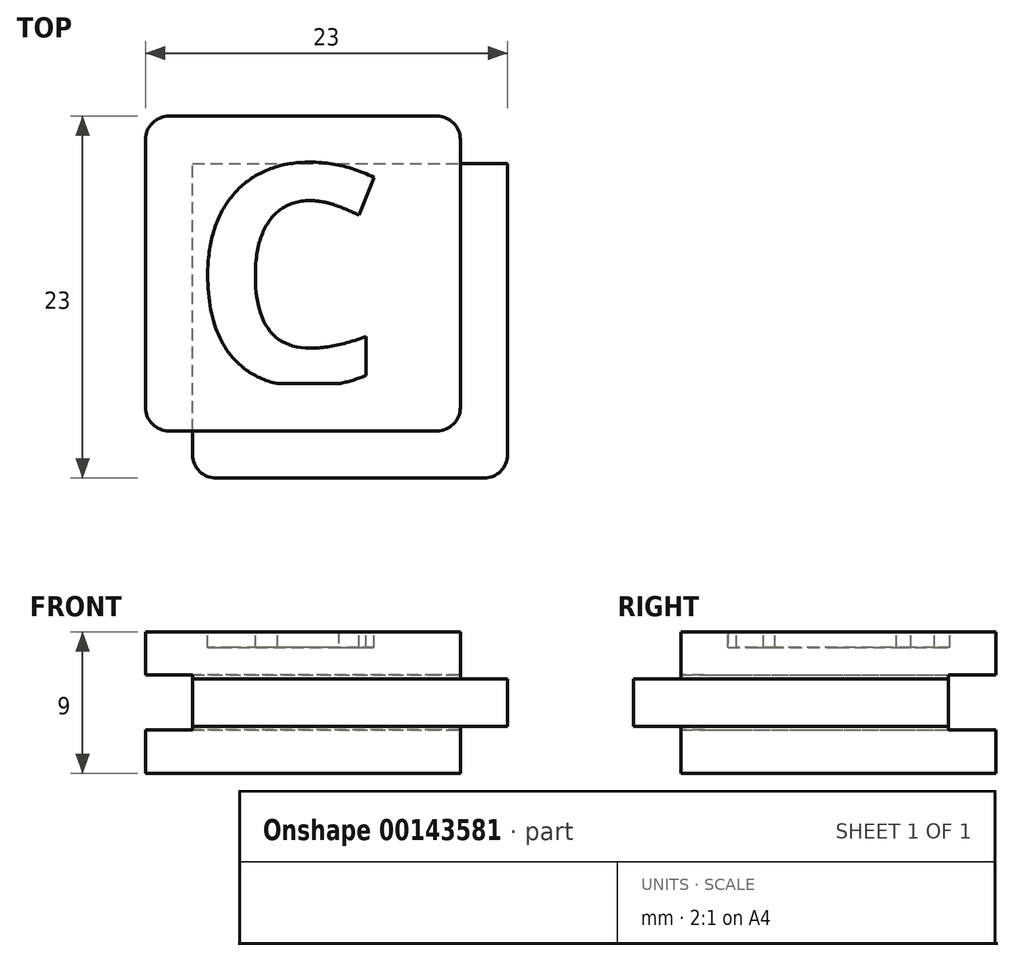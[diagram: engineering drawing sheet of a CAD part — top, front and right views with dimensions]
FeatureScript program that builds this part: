
annotation { "Feature Type Name" : "Feature", "Feature Type Description" : "" }
export const myFeature = defineFeature(function(context is Context, id is Id, definition is map)
    precondition{}
    {
        {
            var Q0;
            Q0=qCreatedBy(makeId("Front.planeOp"),FACE);
            var sketch = newSketch(context, id + "F0", { "sketchPlane" : qUnion([Q0])});
            skLineSegment(sketch, "E0.bottom", {"start": v(10, 4.5) * mm, "end": v(-10, 4.5) * mm});
            skLineSegment(sketch, "E0.top", {"start": v(10, -4.5) * mm, "end": v(-10, -4.5) * mm});
            skLineSegment(sketch, "E0.left", {"start": v(10, 4.5) * mm, "end": v(10, -4.5) * mm});
            skLineSegment(sketch, "E0.right", {"start": v(-10, 4.5) * mm, "end": v(-10, -4.5) * mm});
            skPoint(sketch, "E0.middle", {"position": v(0, 0) * mm});
            skLineSegment(sketch, "E1.bottom", {"start": v(13, 1.5) * mm, "end": v(7, 1.5) * mm});
            skLineSegment(sketch, "E1.top", {"start": v(13, -1.5) * mm, "end": v(7, -1.5) * mm});
            skLineSegment(sketch, "E1.left", {"start": v(13, 1.5) * mm, "end": v(13, -1.5) * mm});
            skLineSegment(sketch, "E1.right", {"start": v(7, 1.5) * mm, "end": v(7, -1.5) * mm});
            skPoint(sketch, "E1.middle", {"position": v(10, 0) * mm});
            skLineSegment(sketch, "E2.bottom", {"start": v(7, 1.5) * mm, "end": v(-7, 1.5) * mm});
            skLineSegment(sketch, "E2.top", {"start": v(7, -1.5) * mm, "end": v(-7, -1.5) * mm});
            skLineSegment(sketch, "E2.right", {"start": v(-7, 1.5) * mm, "end": v(-7, -1.5) * mm});
            skLineSegment(sketch, "E3.bottom", {"start": v(-7, -1.5) * mm, "end": v(-10, -1.5) * mm});
            skLineSegment(sketch, "E3.top", {"start": v(-7, 1.5) * mm, "end": v(-10, 1.5) * mm});
            skLineSegment(sketch, "E3.left", {"start": v(-7, -1.5) * mm, "end": v(-7, 1.5) * mm});
            skLineSegment(sketch, "E3.right", {"start": v(-10, -1.5) * mm, "end": v(-10, 1.5) * mm});
            skSolve(sketch);
        }
        {
            var Q0;
            {var subQ5=sQuery(id+"F0.wireOp",EDGE,"E0.bottom");Q0=makeQuery(id+"F0.imprint","IMPRINT",FACE,{"disambiguationData":[TD([[makeQuery(id+"F0.imprint","IMPRINT",EDGE,{"derivedFrom":subQ5}),1.0]])]});}
            var Q1;
            Q1=makeQuery(id+"F0.imprint","IMPRINT",FACE,{"disambiguationData":[TD([[makeQuery(id+"F0.imprint","IMPRINT",EDGE,{"derivedFrom":sQuery(id+"F0.wireOp",EDGE,"E2.bottom")}),1.0]])]});
            var Q2;
            {var subQ5=sQuery(id+"F0.wireOp",EDGE,"E1.left");Q2=makeQuery(id+"F0.imprint","IMPRINT",FACE,{"disambiguationData":[TD([[makeQuery(id+"F0.imprint","IMPRINT",EDGE,{"derivedFrom":subQ5}),-1.0]])]});}
            var Q3;
            {var subQ5=sQuery(id+"F0.wireOp",EDGE,"E1.right");Q3=makeQuery(id+"F0.imprint","IMPRINT",FACE,{"disambiguationData":[TD([[makeQuery(id+"F0.imprint","IMPRINT",EDGE,{"derivedFrom":subQ5}),1.0]])]});}
            var Q4;
            Q4=makeQuery(id+"F0.imprint","IMPRINT",FACE,{"disambiguationData":[TD([[makeQuery(id+"F0.imprint","IMPRINT",EDGE,{"derivedFrom":sQuery(id+"F0.wireOp",EDGE,"E3.bottom")}),-1.0]])]});
            var Q5;
            {var subQ5=sQuery(id+"F0.wireOp",EDGE,"E0.top");Q5=makeQuery(id+"F0.imprint","IMPRINT",FACE,{"disambiguationData":[TD([[makeQuery(id+"F0.imprint","IMPRINT",EDGE,{"derivedFrom":subQ5}),-1.0]])]});}
            extrude(context, id + "F1", {"entities" : qUnion([Q0, Q1, Q2, Q3, Q4, Q5]), "oppositeDirection" : true, "depth" : 20 * mm});
        }
        {
            var Q0;
            Q0=makeQuery(id+"F0.imprint","IMPRINT",FACE,{"disambiguationData":[TD([[makeQuery(id+"F0.imprint","IMPRINT",EDGE,{"derivedFrom":sQuery(id+"F0.wireOp",EDGE,"E3.bottom")}),-1.0]])]});
            var Q1;
            Q1=makeQuery(id+"F0.imprint","IMPRINT",FACE,{"disambiguationData":[TD([[makeQuery(id+"F0.imprint","IMPRINT",EDGE,{"derivedFrom":sQuery(id+"F0.wireOp",EDGE,"E2.bottom")}),1.0]])]});
            var Q2;
            {var subQ5=sQuery(id+"F0.wireOp",EDGE,"E1.right");Q2=makeQuery(id+"F0.imprint","IMPRINT",FACE,{"disambiguationData":[TD([[makeQuery(id+"F0.imprint","IMPRINT",EDGE,{"derivedFrom":subQ5}),1.0]])]});}
            var Q3;
            {var subQ5=sQuery(id+"F0.wireOp",EDGE,"E1.left");Q3=makeQuery(id+"F0.imprint","IMPRINT",FACE,{"disambiguationData":[TD([[makeQuery(id+"F0.imprint","IMPRINT",EDGE,{"derivedFrom":subQ5}),-1.0]])]});}
            extrude(context, id + "F2", {"entities" : qUnion([Q0, Q1, Q2, Q3]), "operationType" : NewBodyOperationType.ADD, "depth" : 3 * mm});
        }
        {
            var Q0;
            {var subQ0=sQuery(id+"F0.wireOp",EDGE,"E1.left");Q0=makeQuery(id+"F2.boolean.opBoolean","MERGE",FACE,{"derivedFrom":[makeQuery(id+"F1.opExtrude","SWEPT_FACE",FACE,{"disambiguationData":[OSD([subQ0])]}),makeQuery(id+"F2.opExtrude","SWEPT_FACE",FACE,{"disambiguationData":[OSD([subQ0])]})]});}
            var sketch = newSketch(context, id + "F3", { "sketchPlane" : qUnion([Q0])});
            skLineSegment(sketch, "E4.bottom", {"start": v(23, 1.75) * mm, "end": v(17, 1.75) * mm});
            skLineSegment(sketch, "E4.top", {"start": v(23, -1.75) * mm, "end": v(17, -1.75) * mm});
            skLineSegment(sketch, "E4.left", {"start": v(23, 1.75) * mm, "end": v(23, -1.75) * mm});
            skLineSegment(sketch, "E4.right", {"start": v(17, 1.75) * mm, "end": v(17, -1.75) * mm});
            skPoint(sketch, "E4.middle", {"position": v(20, 0) * mm});
            skSolve(sketch);
        }
        {
            var Q0;
            {var subQ1=sQuery(id+"F3.wireOp",EDGE,"E4.bottom");Q0=makeQuery(id+"F3.imprint","IMPRINT",FACE,{"disambiguationData":[TD([[makeQuery(id+"F3.imprint","IMPRINT",EDGE,{"derivedFrom":subQ1}),1.0]])]});}
            var Q1;
            {var subQ1=sQuery(id+"F0.wireOp",EDGE,"E1.left");var subQ8=makeQuery(id+"F1.opExtrude","CAP_EDGE",EDGE,{"disambiguationData":[OSD([subQ1])],"isStart":false});Q1=makeQuery(id+"F3.imprint","IMPRINT",FACE,{"disambiguationData":[TD([[makeQuery(id+"F3.imprint","IMPRINT",EDGE,{"derivedFrom":subQ8}),-1.0]])]});}
            extrude(context, id + "F4", {"entities" : qUnion([Q0, Q1]), "operationType" : NewBodyOperationType.REMOVE, "oppositeDirection" : true, "depth" : 100 * mm});
        }
        {
            var Q0;
            Q0=makeQuery(id+"F4.boolean.opBoolean","COPY",FACE,{"derivedFrom":makeQuery(id+"F4.opExtrude","SWEPT_FACE",FACE,{"disambiguationData":[OSD([sQuery(id+"F3.wireOp",EDGE,"E4.right")])]})});
            var sketch = newSketch(context, id + "F5", { "sketchPlane" : qUnion([Q0])});
            skLineSegment(sketch, "E5.bottom", {"start": v(13, 1.75) * mm, "end": v(7, 1.75) * mm});
            skLineSegment(sketch, "E5.top", {"start": v(13, -1.75) * mm, "end": v(7, -1.75) * mm});
            skLineSegment(sketch, "E5.left", {"start": v(13, 1.75) * mm, "end": v(13, -1.75) * mm});
            skLineSegment(sketch, "E5.right", {"start": v(7, 1.75) * mm, "end": v(7, -1.75) * mm});
            skPoint(sketch, "E5.middle", {"position": v(10, 0) * mm});
            skSolve(sketch);
        }
        {
            var Q0;
            {var subQ3=sQuery(id+"F5.wireOp",EDGE,"E5.left");Q0=makeQuery(id+"F5.imprint","IMPRINT",FACE,{"disambiguationData":[TD([[makeQuery(id+"F5.imprint","IMPRINT",EDGE,{"derivedFrom":subQ3}),-1.0]])]});}
            var Q1;
            {var subQ4=sQuery(id+"F5.wireOp",EDGE,"E5.right");Q1=makeQuery(id+"F5.imprint","IMPRINT",FACE,{"disambiguationData":[TD([[makeQuery(id+"F5.imprint","IMPRINT",EDGE,{"derivedFrom":subQ4}),1.0]])]});}
            extrude(context, id + "F6", {"entities" : qUnion([Q0, Q1]), "operationType" : NewBodyOperationType.REMOVE, "oppositeDirection" : true, "depth" : 100 * mm});
        }
        {
            var Q0;
            Q0=makeQuery(id+"F6.boolean.opBoolean","INTERSECT",EDGE,{"derivedFrom":[makeQuery(id+"F2.opExtrude","CAP_FACE",FACE,{"disambiguationData":[OSD([sQuery(id+"F0.wireOp",EDGE,"E1.bottom"),sQuery(id+"F0.wireOp",EDGE,"E1.top"),sQuery(id+"F0.wireOp",EDGE,"E1.left"),sQuery(id+"F0.wireOp",EDGE,"E2.bottom"),sQuery(id+"F0.wireOp",EDGE,"E2.top"),sQuery(id+"F0.wireOp",EDGE,"E3.bottom"),sQuery(id+"F0.wireOp",EDGE,"E3.top"),sQuery(id+"F0.wireOp",EDGE,"E3.right")])],"isStart":false}),makeQuery(id+"F6.opExtrude","SWEPT_FACE",FACE,{"disambiguationData":[OSD([sQuery(id+"F5.wireOp",EDGE,"E5.right")])]})]});
            var Q1;
            Q1=makeQuery(id+"F2.opExtrude","CAP_EDGE",EDGE,{"disambiguationData":[OSD([sQuery(id+"F0.wireOp",EDGE,"E1.left")])],"isStart":false});
            var Q2;
            {var subQ0=sQuery(id+"F0.wireOp",EDGE,"E0.left");Q2=makeQuery(id+"F1.opExtrude","CAP_EDGE",EDGE,{"disambiguationData":[OSD([subQ0]),TDD([makeQuery(id+"F0.imprint","IMPRINT",EDGE,{"disambiguationData":[TD([[makeQuery(id+"F0.imprint","INTERSECT",VERTEX,{"derivedFrom":[sQuery(id+"F0.wireOp",EDGE,"E0.bottom"),subQ0]}),-1.0]])],"derivedFrom":subQ0})])],"isStart":true});}
            var Q3;
            {var subQ0=sQuery(id+"F0.wireOp",EDGE,"E0.left");Q3=makeQuery(id+"F1.opExtrude","CAP_EDGE",EDGE,{"disambiguationData":[OSD([subQ0]),TDD([makeQuery(id+"F0.imprint","IMPRINT",EDGE,{"disambiguationData":[TD([[makeQuery(id+"F0.imprint","INTERSECT",VERTEX,{"derivedFrom":[sQuery(id+"F0.wireOp",EDGE,"E0.top"),subQ0]}),1.0]])],"derivedFrom":subQ0})])],"isStart":true});}
            var Q4;
            {var subQ0=sQuery(id+"F0.wireOp",EDGE,"E3.right");var subQ1=sQuery(id+"F0.wireOp",EDGE,"E0.right");var subQ3=sQuery(id+"F0.wireOp",EDGE,"E0.top");Q4=makeQuery(id+"F2.boolean.opBoolean","SPLIT",EDGE,{"disambiguationData":[TD([makeQuery(id+"F1.opExtrude","SWEPT_FACE",FACE,{"disambiguationData":[OSD([subQ3])]})])],"derivedFrom":makeQuery(id+"F1.opExtrude","CAP_EDGE",EDGE,{"disambiguationData":[OSD([subQ1,subQ0])],"isStart":true})});}
            var Q5;
            {var subQ1=sQuery(id+"F0.wireOp",EDGE,"E3.right");var subQ2=sQuery(id+"F0.wireOp",EDGE,"E0.right");var subQ3=sQuery(id+"F0.wireOp",EDGE,"E0.bottom");Q5=makeQuery(id+"F2.boolean.opBoolean","SPLIT",EDGE,{"disambiguationData":[TD([makeQuery(id+"F1.opExtrude","SWEPT_FACE",FACE,{"disambiguationData":[OSD([subQ3])]})])],"derivedFrom":makeQuery(id+"F1.opExtrude","CAP_EDGE",EDGE,{"disambiguationData":[OSD([subQ2,subQ1])],"isStart":true})});}
            var Q6;
            Q6=makeQuery(id+"F6.boolean.opBoolean","COPY",EDGE,{"derivedFrom":makeQuery(id+"F6.opExtrude","CAP_EDGE",EDGE,{"disambiguationData":[OSD([sQuery(id+"F5.wireOp",EDGE,"E5.right")])],"isStart":true})});
            var Q7;
            {var subQ0=sQuery(id+"F0.wireOp",EDGE,"E3.right");var subQ1=sQuery(id+"F0.wireOp",EDGE,"E0.right");var subQ2=sQuery(id+"F0.wireOp",EDGE,"E0.bottom");Q7=makeQuery(id+"F4.boolean.opBoolean","SPLIT",EDGE,{"disambiguationData":[TD([makeQuery(id+"F1.opExtrude","SWEPT_FACE",FACE,{"disambiguationData":[OSD([subQ2])]})])],"derivedFrom":makeQuery(id+"F1.opExtrude","CAP_EDGE",EDGE,{"disambiguationData":[OSD([subQ1,subQ0])],"isStart":false})});}
            var Q8;
            {var subQ0=sQuery(id+"F0.wireOp",EDGE,"E3.right");var subQ1=sQuery(id+"F0.wireOp",EDGE,"E0.right");var subQ2=sQuery(id+"F0.wireOp",EDGE,"E0.top");Q8=makeQuery(id+"F4.boolean.opBoolean","SPLIT",EDGE,{"disambiguationData":[TD([makeQuery(id+"F1.opExtrude","SWEPT_FACE",FACE,{"disambiguationData":[OSD([subQ2])]})])],"derivedFrom":makeQuery(id+"F1.opExtrude","CAP_EDGE",EDGE,{"disambiguationData":[OSD([subQ1,subQ0])],"isStart":false})});}
            var Q9;
            Q9=makeQuery(id+"F4.boolean.opBoolean","COPY",EDGE,{"derivedFrom":makeQuery(id+"F4.opExtrude","CAP_EDGE",EDGE,{"disambiguationData":[OSD([sQuery(id+"F3.wireOp",EDGE,"E4.right")])],"isStart":true})});
            var Q10;
            {var subQ0=sQuery(id+"F0.wireOp",EDGE,"E0.left");Q10=makeQuery(id+"F1.opExtrude","CAP_EDGE",EDGE,{"disambiguationData":[OSD([subQ0]),TDD([makeQuery(id+"F0.imprint","IMPRINT",EDGE,{"disambiguationData":[TD([[makeQuery(id+"F0.imprint","INTERSECT",VERTEX,{"derivedFrom":[sQuery(id+"F0.wireOp",EDGE,"E0.bottom"),subQ0]}),-1.0]])],"derivedFrom":subQ0})])],"isStart":false});}
            var Q11;
            {var subQ0=sQuery(id+"F0.wireOp",EDGE,"E0.left");Q11=makeQuery(id+"F1.opExtrude","CAP_EDGE",EDGE,{"disambiguationData":[OSD([subQ0]),TDD([makeQuery(id+"F0.imprint","IMPRINT",EDGE,{"disambiguationData":[TD([[makeQuery(id+"F0.imprint","INTERSECT",VERTEX,{"derivedFrom":[sQuery(id+"F0.wireOp",EDGE,"E0.top"),subQ0]}),1.0]])],"derivedFrom":subQ0})])],"isStart":false});}
            fillet(context, id + "F7", {"entities" : qUnion([Q0, Q1, Q2, Q3, Q4, Q5, Q6, Q7, Q8, Q9, Q10, Q11]), "radius" : 1.5 * mm, "tangentPropagation" : true, "allowEdgeOverflow" : false});
        }
        {
            var Q0;
            Q0=makeQuery(id+"F1.opExtrude","SWEPT_FACE",FACE,{"disambiguationData":[OSD([sQuery(id+"F0.wireOp",EDGE,"E0.bottom")])]});
            var sketch = newSketch(context, id + "F8", { "sketchPlane" : qUnion([Q0])});
            skText(sketch, "E6", { "text": "C", "fontName": "OpenSans-Bold.ttf"});
            skLineSegment(sketch, "E7.0", {"start": v(9.67, 3) * mm, "end": v(-11.07, 3) * mm});
            const initialGuessF8  = {"E6": [-0.00718, 0.003, 1, 0, 0.014]};
            skSetInitialGuess(sketch, initialGuessF8);
            skSolve(sketch);
        }
        {
            var Q0;
            Q0=makeQuery(id+"F8.imprint","IMPRINT",FACE,{"disambiguationData":[TD([[makeQuery(id+"F8.imprint","IMPRINT",EDGE,{"derivedFrom":sQuery(id+"F8.wireOp",EDGE,"E6.sketch_text.stroke-0")}),-1.0]])]});
            extrude(context, id + "F9", {"entities" : qUnion([Q0]), "operationType" : NewBodyOperationType.REMOVE, "oppositeDirection" : true, "depth" : 1 * mm});
        }
    });
